# Revit family: WWW_A3-Full-Arch-1248-CHB3
name_source: partatom
category: Windows
revit_build: Autodesk Revit 2016 (Build: 20150220_1215(x64)
units: mm (PartAtom-declared; Revit-internal decimal feet)

## family parameters
Always vertical = Yes
Cut with Voids When Loaded = No
Host = Wall
Room Calculation Point = No
Shared = No

## types (1)
- 1248 x 1116 CHB3
    Assembly Code = B2020130
    Default Sill Height = 1052 mm  [stored 3.45144 ft]
    Frame Material = Frame Material
    Head height = 2300 mm
    Height = 1248 mm  [stored 4.09449 ft]
    Manufacturer = AC Shopfitters (Windows)
    Manufacturer Code = CHB3
    Model = Full Arch
    Type Comments = series iv frame profile
    URL = www.acdoors.co.za
    Wall Closure = By host
    Width = 1116 mm

note: [stored X ft] marks values corroborated as IEEE doubles in the binary element streams (Revit-internal decimal feet)

## geometry (parser evidence)
native form markers: Sweep x9
no freeform markers — native parametric forms only
